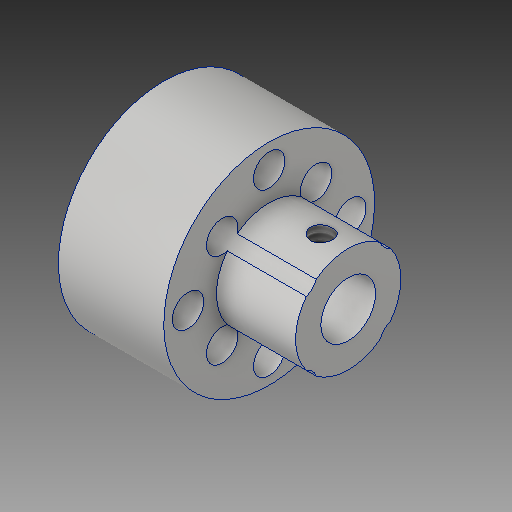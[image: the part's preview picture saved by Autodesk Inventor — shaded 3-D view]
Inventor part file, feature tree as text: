
AUTODESK INVENTOR PART (.ipt)
format: ipt  version: 2017 (Build 210142000, 142)  size: 186,368 bytes
history: native  units: in
note: dims shown in document units (in); Inventor stores cm internally (conversion verified against a paired STEP export)
features: sketch x3, hole x3, extrude x2, plane x1, projected_geometry x1
ambient origin geometry x8: Origin, YZ Plane, XZ Plane, XY Plane, X Axis, Y Axis, Z Axis, Center Point
bodies: Solid1 (feature_tree)
feature tree (10):
  sketch  "Sketch1"  dims[d0=1.0in d6=45.0deg]
  extrude  "Extrusion1"  TaperAngle=45.0deg  [1 undecoded]
  extrude  "Extrusion2"  Depth=0.5in TaperAngle=0.0deg
  hole  "Hole1"  [1 undecoded]
  hole  "Hole2"  [1 undecoded]
  plane  "Work Plane2"
  hole  "Hole3"  [1 undecoded]
  sketch  "Sketch2"  dims[d15=0.26in d16=0.5in d17=0.0in]
  sketch  "Sketch5"  dims[d18=0.5in d19=0.375in d20=0.0in d21=1.5748in d23=360.0deg d25=0.385in d26=1.5748in d28=360.0deg d30=0.15in d31=0.75in d32=0.375in d33=0.25in d34=0.5635in d35=1.0in d36=0.8108in d37=0.15in d38=0.75in d39=0.375in d40=0.25in d41=0.5635in d42=1.0in d43=0.8108in d46=0.125in d47=0.104in d48=0.276in d49=0.375in d50=0.25in d51=0.5635in d52=0.432in d53=0.8108in]
  projected_geometry  "Projected Loop1"
note: 4 required parameter values undecoded (feature->parameter linkage not recoverable at this tier; creation-order binding heuristic only, values carry confidence <= 0.55)
